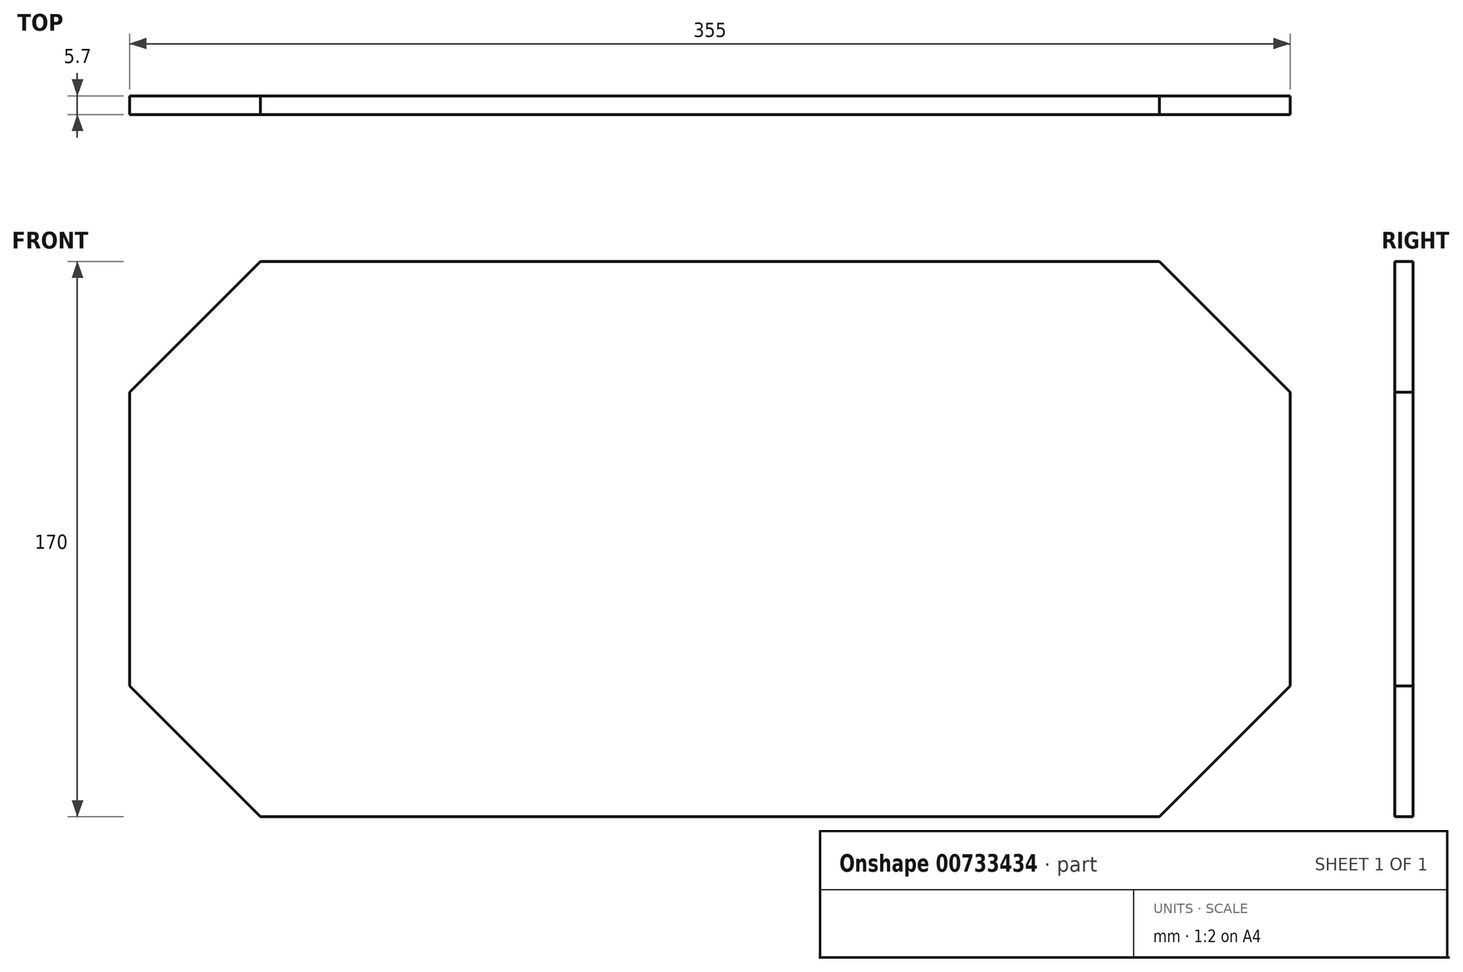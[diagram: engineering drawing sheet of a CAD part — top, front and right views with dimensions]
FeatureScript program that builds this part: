
annotation { "Feature Type Name" : "Feature", "Feature Type Description" : "" }
export const myFeature = defineFeature(function(context is Context, id is Id, definition is map)
    precondition{}
    {
        {
            var Q0;
            Q0=qCreatedBy(makeId("Front.planeOp"),FACE);
            var sketch = newSketch(context, id + "F0", { "sketchPlane" : qUnion([Q0])});
            skLineSegment(sketch, "E0.bottom", {"start": v(177.5, -85) * mm, "end": v(-177.5, -85) * mm});
            skLineSegment(sketch, "E0.top", {"start": v(177.5, 85) * mm, "end": v(-177.5, 85) * mm});
            skLineSegment(sketch, "E0.left", {"start": v(177.5, -85) * mm, "end": v(177.5, 85) * mm});
            skLineSegment(sketch, "E0.right", {"start": v(-177.5, -85) * mm, "end": v(-177.5, 85) * mm});
            skPoint(sketch, "E0.middle", {"position": v(0, 0) * mm});
            skSolve(sketch);
        }
        {
            var Q0;
            Q0 = qSketchRegion(id + "F0", true);
            extrude(context, id + "F1", {"entities" : qUnion([Q0]), "depth" : 5.7 * mm, "offsetDistance" : 25 * mm});
        }
        {
            var Q0;
            Q0=makeQuery(id+"F1.opExtrude","CAP_FACE",FACE,{"disambiguationData":[OSD([sQuery(id+"F0.wireOp",EDGE,"E0.bottom"),sQuery(id+"F0.wireOp",EDGE,"E0.top"),sQuery(id+"F0.wireOp",EDGE,"E0.left"),sQuery(id+"F0.wireOp",EDGE,"E0.right")])],"isStart":false});
            var sketch = newSketch(context, id + "F2", { "sketchPlane" : qUnion([Q0])});
            skLineSegment(sketch, "E1", {"start": v(-137.5, 85) * mm, "end": v(-177.5, 45) * mm});
            skLineSegment(sketch, "E2", {"start": v(-177.5, 45) * mm, "end": v(-177.5, 85) * mm});
            skLineSegment(sketch, "E3", {"start": v(-177.5, 85) * mm, "end": v(-137.5, 85) * mm});
            skLineSegment(sketch, "E4", {"start": v(137.5, 85) * mm, "end": v(177.5, 45) * mm});
            skLineSegment(sketch, "E5", {"start": v(177.5, 45) * mm, "end": v(177.5, 85) * mm});
            skLineSegment(sketch, "E6", {"start": v(177.5, 85) * mm, "end": v(137.5, 85) * mm});
            skLineSegment(sketch, "E7", {"start": v(177.5, -45) * mm, "end": v(137.5, -85) * mm});
            skLineSegment(sketch, "E8", {"start": v(137.5, -85) * mm, "end": v(177.5, -85) * mm});
            skLineSegment(sketch, "E9", {"start": v(177.5, -85) * mm, "end": v(177.5, -45) * mm});
            skLineSegment(sketch, "E10", {"start": v(-177.5, -85) * mm, "end": v(-137.5, -85) * mm});
            skLineSegment(sketch, "E11", {"start": v(-137.5, -85) * mm, "end": v(-177.5, -45) * mm});
            skLineSegment(sketch, "E12", {"start": v(-177.5, -45) * mm, "end": v(-177.5, -85) * mm});
            skSolve(sketch);
        }
        {
            var Q0;
            Q0 = qSketchRegion(id + "F2", true);
            extrude(context, id + "F3", {"entities" : qUnion([Q0]), "operationType" : NewBodyOperationType.REMOVE, "endBound" : BoundingType.UP_TO_NEXT, "oppositeDirection" : true, "depth" : 25 * mm, "offsetDistance" : 25 * mm});
        }
    });
